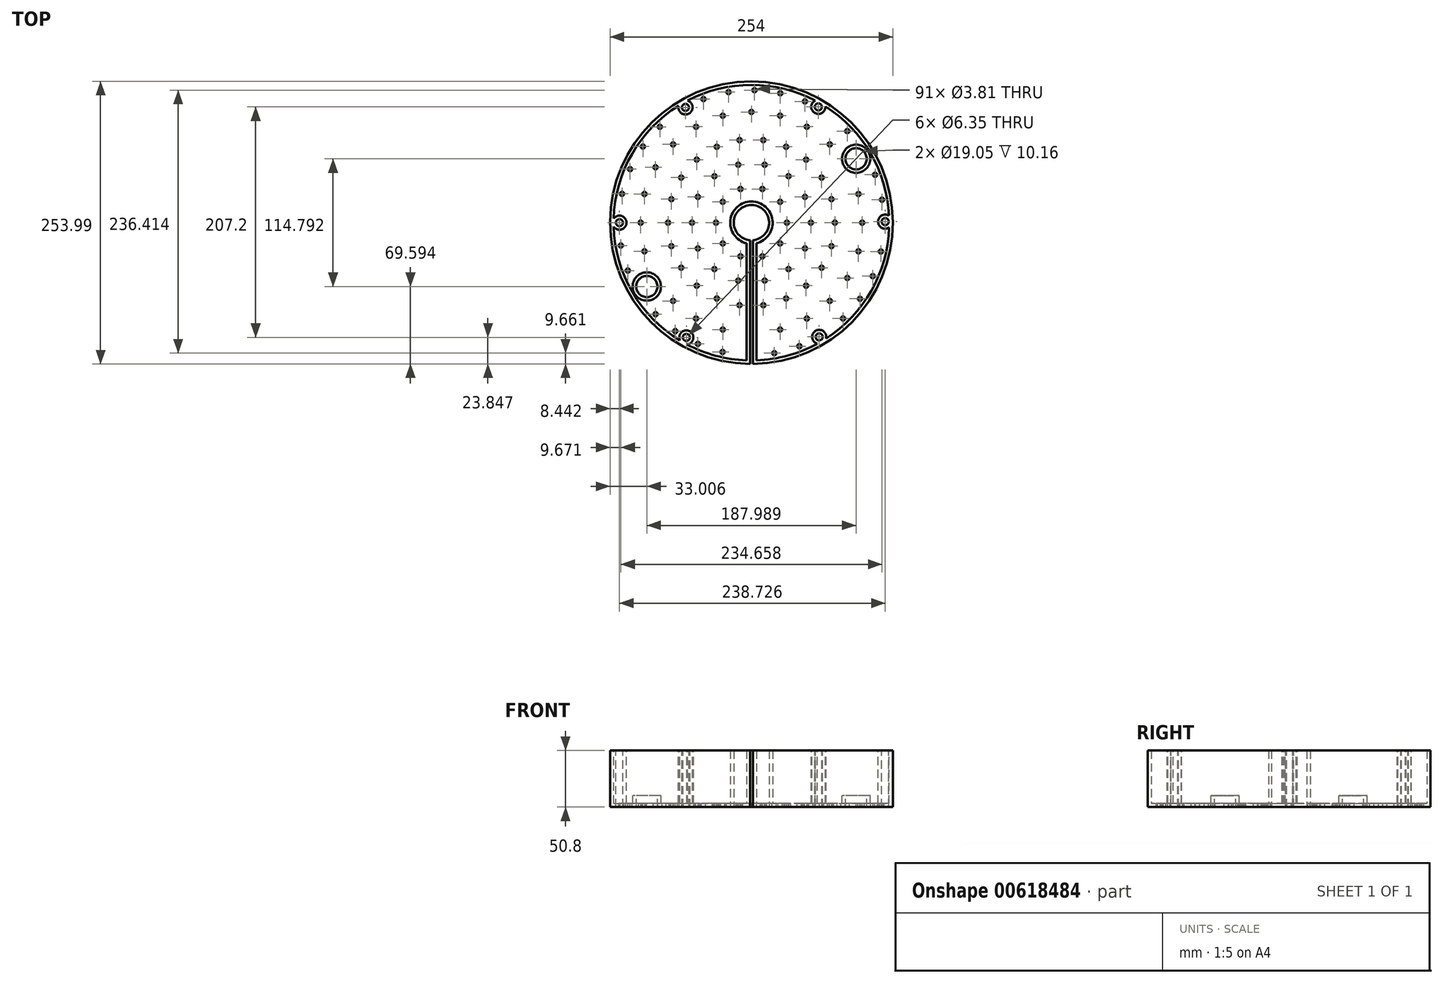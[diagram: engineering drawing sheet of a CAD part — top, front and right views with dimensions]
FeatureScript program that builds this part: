
annotation { "Feature Type Name" : "Feature", "Feature Type Description" : "" }
export const myFeature = defineFeature(function(context is Context, id is Id, definition is map)
    precondition{}
    {
        {
            var Q0;
            Q0=qCreatedBy(makeId("Top.planeOp"),FACE);
            var sketch = newSketch(context, id + "F0", { "sketchPlane" : qUnion([Q0])});
            skLineSegment(sketch, "E0.left", {"start": v(0, 0) * mm, "end": v(0, 0) * mm});
            skArc(sketch, "E1", {"start": v(1.27, -127) * mm, "mid": v(0, 127) * mm, "end": v(-1.27, -127) * mm});
            skArc(sketch, "E2", {"start": v(1.27, -15.82) * mm, "mid": v(0, 15.87) * mm, "end": v(-1.27, -15.82) * mm});
            skLineSegment(sketch, "E3", {"start": v(0, 0) * mm, "end": v(0, -127) * mm, "construction": true});
            skLineSegment(sketch, "E4", {"start": v(-1.27, -15.82) * mm, "end": v(-1.27, -127) * mm});
            skLineSegment(sketch, "E5", {"start": v(1.27, -15.82) * mm, "end": v(1.27, -127) * mm});
            skSolve(sketch);
        }
        {
            var Q0;
            Q0 = qSketchRegion(id + "F0", true);
            extrude(context, id + "F1", {"entities" : qUnion([Q0]), "depth" : 50.8 * mm, "offsetDistance" : 25.4 * mm});
        }
        {
            var Q0;
            Q0=makeQuery(id+"F1.opExtrude","CAP_FACE",FACE,{"disambiguationData":[OSD([sQuery(id+"F0.wireOp",EDGE,"E1"),sQuery(id+"F0.wireOp",EDGE,"E2"),sQuery(id+"F0.wireOp",EDGE,"E4"),sQuery(id+"F0.wireOp",EDGE,"E5")])],"isStart":false});
            var sketch = newSketch(context, id + "F2", { "sketchPlane" : qUnion([Q0])});
            skPoint(sketch, "E6", {"position": v(-118.56, 0) * mm});
            skPoint(sketch, "E7.1.0", {"position": v(-58.48, -103.14) * mm});
            skPoint(sketch, "E7.2.0", {"position": v(60.88, -102.69) * mm});
            skPoint(sketch, "E7.3.0", {"position": v(120.17, 0.91) * mm});
            skPoint(sketch, "E7.4.0", {"position": v(60.09, 104.06) * mm});
            skPoint(sketch, "E7.5.0", {"position": v(-59.27, 103.6) * mm});
            skPoint(sketch, "E7.center", {"position": v(0.8, 0.46) * mm});
            skPoint(sketch, "E8.center", {"position": v(0, 0) * mm});
            skSolve(sketch);
        }
        {
            var Q0;
            Q0=sQuery(id+"F2.wireOp",VERTEX,"E6");
            var Q1;
            Q1=sQuery(id+"F2.wireOp",VERTEX,"E7.5.0");
            var Q2;
            Q2=sQuery(id+"F2.wireOp",VERTEX,"E7.4.0");
            var Q3;
            Q3=sQuery(id+"F2.wireOp",VERTEX,"E7.3.0");
            var Q4;
            Q4=sQuery(id+"F2.wireOp",VERTEX,"E7.2.0");
            var Q5;
            Q5=sQuery(id+"F2.wireOp",VERTEX,"E7.1.0");
            var Q6;
            Q6=makeQuery(id+"F1.opExtrude","SWEPT_BODY",BODY,{"disambiguationData":[OSD([sQuery(id+"F0.wireOp",EDGE,"E1"),sQuery(id+"F0.wireOp",EDGE,"E2"),sQuery(id+"F0.wireOp",EDGE,"E4"),sQuery(id+"F0.wireOp",EDGE,"E5")])]});
            hole(context, id + "F3", {"style" : HoleStyle.SIMPLE, "endStyle" : HoleEndStyle.THROUGH, "holeDiameter" : 6.35 * mm, "majorDiameter" : 6.35 * mm, "isTappedThrough" : true, "tappedDepth" : 12.7 * mm, "tapClearance" : 3, "startFromSketch" : true, "locations" : qUnion([Q0, Q1, Q2, Q3, Q4, Q5]), "scope" : qUnion([Q6])});
        }
        {
            var Q0;
            Q0=makeQuery(id+"F1.opExtrude","CAP_FACE",FACE,{"disambiguationData":[OSD([sQuery(id+"F0.wireOp",EDGE,"E1"),sQuery(id+"F0.wireOp",EDGE,"E2"),sQuery(id+"F0.wireOp",EDGE,"E4"),sQuery(id+"F0.wireOp",EDGE,"E5")])],"isStart":false});
            var sketch = newSketch(context, id + "F4", { "sketchPlane" : qUnion([Q0])});
            skPoint(sketch, "E9", {"position": v(-94, -57.4) * mm});
            skPoint(sketch, "E10.1.0", {"position": v(94, 57.4) * mm});
            skPoint(sketch, "E10.center", {"position": v(0, 0) * mm});
            skSolve(sketch);
        }
        {
            var Q0;
            Q0=sQuery(id+"F4.wireOp",VERTEX,"E9");
            var Q1;
            Q1=sQuery(id+"F4.wireOp",VERTEX,"E10.1.0");
            var Q2;
            Q2=makeQuery(id+"F1.opExtrude","SWEPT_BODY",BODY,{"disambiguationData":[OSD([sQuery(id+"F0.wireOp",EDGE,"E1"),sQuery(id+"F0.wireOp",EDGE,"E2"),sQuery(id+"F0.wireOp",EDGE,"E4"),sQuery(id+"F0.wireOp",EDGE,"E5")])]});
            hole(context, id + "F5", {"style" : HoleStyle.SIMPLE, "endStyle" : HoleEndStyle.THROUGH, "holeDiameter" : 19.05 * mm, "majorDiameter" : 6.35 * mm, "isTappedThrough" : true, "tappedDepth" : 12.7 * mm, "tapClearance" : 3, "startFromSketch" : true, "locations" : qUnion([Q0, Q1]), "scope" : qUnion([Q2])});
        }
        {
            var Q0;
            Q0=makeQuery(id+"F1.opExtrude","CAP_FACE",FACE,{"disambiguationData":[OSD([sQuery(id+"F0.wireOp",EDGE,"E1"),sQuery(id+"F0.wireOp",EDGE,"E2"),sQuery(id+"F0.wireOp",EDGE,"E4"),sQuery(id+"F0.wireOp",EDGE,"E5")])],"isStart":false});
            shell(context, id + "F6", {"entities" : qUnion([Q0]), "thickness" : 3.17 * mm});
        }
        {
            var Q0;
            {var subQ0=sQuery(id+"F0.wireOp",EDGE,"E5");var subQ1=sQuery(id+"F0.wireOp",EDGE,"E4");var subQ2=sQuery(id+"F0.wireOp",EDGE,"E2");var subQ3=sQuery(id+"F0.wireOp",EDGE,"E1");Q0=makeQuery(id+"F6.opShell","OFFSET_FACE",FACE,{"disambiguationData":[OSD([subQ3,subQ2,subQ1,subQ0]),TDD([makeQuery(id+"F1.opExtrude","CAP_FACE",FACE,{"disambiguationData":[OSD([subQ3,subQ2,subQ1,subQ0])],"isStart":false})]),OD(0.0)]});}
            var Q1;
            {var subQ0=sQuery(id+"F0.wireOp",EDGE,"E5");var subQ1=sQuery(id+"F0.wireOp",EDGE,"E4");var subQ2=sQuery(id+"F0.wireOp",EDGE,"E2");var subQ3=sQuery(id+"F0.wireOp",EDGE,"E1");Q1=makeQuery(id+"F6.opShell","OFFSET_FACE",FACE,{"disambiguationData":[OSD([subQ3,subQ2,subQ1,subQ0]),TDD([makeQuery(id+"F1.opExtrude","CAP_FACE",FACE,{"disambiguationData":[OSD([subQ3,subQ2,subQ1,subQ0])],"isStart":false})]),OD(1.0)]});}
            extrude(context, id + "F7", {"entities" : qUnion([Q0, Q1]), "operationType" : NewBodyOperationType.REMOVE, "oppositeDirection" : true, "depth" : 25.4 * mm, "offsetDistance" : 25.4 * mm});
        }
        {
            var Q0;
            {var subQ0=sQuery(id+"F0.wireOp",EDGE,"E5");var subQ1=sQuery(id+"F0.wireOp",EDGE,"E4");var subQ2=sQuery(id+"F0.wireOp",EDGE,"E2");var subQ3=sQuery(id+"F0.wireOp",EDGE,"E1");Q0=makeQuery(id+"F7.boolean.opBoolean","COPY",FACE,{"derivedFrom":makeQuery(id+"F7.opExtrude","CAP_FACE",FACE,{"disambiguationData":[OSD([subQ3,subQ2,subQ1,subQ0]),TDD([makeQuery(id+"F6.opShell","OFFSET_FACE",FACE,{"disambiguationData":[OSD([subQ3,subQ2,subQ1,subQ0]),TDD([makeQuery(id+"F1.opExtrude","CAP_FACE",FACE,{"disambiguationData":[OSD([subQ3,subQ2,subQ1,subQ0])],"isStart":false})]),OD(0.0)]})])],"isStart":false})});}
            var Q1;
            {var subQ0=sQuery(id+"F0.wireOp",EDGE,"E5");var subQ1=sQuery(id+"F0.wireOp",EDGE,"E4");var subQ2=sQuery(id+"F0.wireOp",EDGE,"E2");var subQ3=sQuery(id+"F0.wireOp",EDGE,"E1");Q1=makeQuery(id+"F7.boolean.opBoolean","COPY",FACE,{"derivedFrom":makeQuery(id+"F7.opExtrude","CAP_FACE",FACE,{"disambiguationData":[OSD([subQ3,subQ2,subQ1,subQ0]),TDD([makeQuery(id+"F6.opShell","OFFSET_FACE",FACE,{"disambiguationData":[OSD([subQ3,subQ2,subQ1,subQ0]),TDD([makeQuery(id+"F1.opExtrude","CAP_FACE",FACE,{"disambiguationData":[OSD([subQ3,subQ2,subQ1,subQ0])],"isStart":false})]),OD(1.0)]})])],"isStart":false})});}
            extrude(context, id + "F8", {"entities" : qUnion([Q0, Q1]), "operationType" : NewBodyOperationType.REMOVE, "oppositeDirection" : true, "depth" : 15.24 * mm, "offsetDistance" : 25.4 * mm});
        }
        {
            var Q0;
            {var subQ0=sQuery(id+"F0.wireOp",EDGE,"E5");var subQ1=sQuery(id+"F0.wireOp",EDGE,"E4");var subQ2=sQuery(id+"F0.wireOp",EDGE,"E2");var subQ3=sQuery(id+"F0.wireOp",EDGE,"E1");Q0=makeQuery(id+"F6.opShell","OFFSET_FACE",FACE,{"disambiguationData":[OSD([subQ3,subQ2,subQ1,subQ0]),TDD([makeQuery(id+"F1.opExtrude","CAP_FACE",FACE,{"disambiguationData":[OSD([subQ3,subQ2,subQ1,subQ0])],"isStart":true})])]});}
            var sketch = newSketch(context, id + "F9", { "sketchPlane" : qUnion([Q0])});
            skPoint(sketch, "E11", {"position": v(-31.83, 0) * mm});
            skPoint(sketch, "E12.1.0", {"position": v(-25.75, -18.71) * mm});
            skPoint(sketch, "E12.2.0", {"position": v(-9.84, -30.27) * mm});
            skPoint(sketch, "E12.3.0", {"position": v(9.84, -30.27) * mm});
            skPoint(sketch, "E12.4.0", {"position": v(25.75, -18.71) * mm});
            skPoint(sketch, "E12.5.0", {"position": v(31.83, 0) * mm});
            skPoint(sketch, "E12.6.0", {"position": v(25.75, 18.71) * mm});
            skPoint(sketch, "E12.7.0", {"position": v(9.84, 30.27) * mm});
            skPoint(sketch, "E12.8.0", {"position": v(-9.84, 30.27) * mm});
            skPoint(sketch, "E12.center", {"position": v(0, 0) * mm});
            skPoint(sketch, "E13.0.9.0", {"position": v(-25.75, 18.71) * mm});
            skPoint(sketch, "E14", {"position": v(-53.39, 0) * mm});
            skPoint(sketch, "E15.1.0", {"position": v(-48.1, -23.16) * mm});
            skPoint(sketch, "E15.2.0", {"position": v(-33.29, -41.74) * mm});
            skPoint(sketch, "E15.3.0", {"position": v(-11.88, -52.05) * mm});
            skPoint(sketch, "E15.4.0", {"position": v(11.88, -52.05) * mm});
            skPoint(sketch, "E15.5.0", {"position": v(33.29, -41.74) * mm});
            skPoint(sketch, "E15.6.0", {"position": v(48.1, -23.16) * mm});
            skPoint(sketch, "E15.7.0", {"position": v(53.39, 0) * mm});
            skPoint(sketch, "E15.8.0", {"position": v(48.1, 23.16) * mm});
            skPoint(sketch, "E15.9.0", {"position": v(33.29, 41.74) * mm});
            skPoint(sketch, "E15.10.0", {"position": v(11.88, 52.05) * mm});
            skPoint(sketch, "E15.11.0", {"position": v(-11.88, 52.05) * mm});
            skPoint(sketch, "E15.12.0", {"position": v(-33.29, 41.74) * mm});
            skPoint(sketch, "E15.13.0", {"position": v(-48.1, 23.16) * mm});
            skPoint(sketch, "E16", {"position": v(-74.94, 0) * mm});
            skPoint(sketch, "E17.1.0", {"position": v(-71.9, -21.11) * mm});
            skPoint(sketch, "E17.2.0", {"position": v(-63.05, -40.52) * mm});
            skPoint(sketch, "E17.3.0", {"position": v(-49.08, -56.64) * mm});
            skPoint(sketch, "E17.4.0", {"position": v(-31.13, -68.17) * mm});
            skPoint(sketch, "E17.5.0", {"position": v(-10.67, -74.18) * mm});
            skPoint(sketch, "E17.6.0", {"position": v(10.67, -74.18) * mm});
            skPoint(sketch, "E17.7.0", {"position": v(31.13, -68.17) * mm});
            skPoint(sketch, "E17.8.0", {"position": v(49.08, -56.64) * mm});
            skPoint(sketch, "E17.9.0", {"position": v(63.05, -40.52) * mm});
            skPoint(sketch, "E17.10.0", {"position": v(71.9, -21.11) * mm});
            skPoint(sketch, "E17.11.0", {"position": v(74.94, 0) * mm});
            skPoint(sketch, "E17.12.0", {"position": v(71.9, 21.11) * mm});
            skPoint(sketch, "E17.13.0", {"position": v(63.05, 40.52) * mm});
            skPoint(sketch, "E17.14.0", {"position": v(49.08, 56.64) * mm});
            skPoint(sketch, "E17.15.0", {"position": v(31.13, 68.17) * mm});
            skPoint(sketch, "E17.16.0", {"position": v(10.67, 74.18) * mm});
            skPoint(sketch, "E17.17.0", {"position": v(-10.67, 74.18) * mm});
            skPoint(sketch, "E17.18.0", {"position": v(-31.13, 68.17) * mm});
            skPoint(sketch, "E17.19.0", {"position": v(-49.08, 56.64) * mm});
            skPoint(sketch, "E18.0.20.0", {"position": v(-63.05, 40.52) * mm});
            skPoint(sketch, "E18.0.21.0", {"position": v(-71.9, 21.11) * mm});
            skPoint(sketch, "E19", {"position": v(-99.5, 0) * mm});
            skPoint(sketch, "E20.1.0", {"position": v(-96.12, -25.75) * mm});
            skPoint(sketch, "E20.3.0", {"position": v(-70.36, -70.36) * mm});
            skPoint(sketch, "E20.4.0", {"position": v(-49.75, -86.18) * mm});
            skPoint(sketch, "E20.5.0", {"position": v(-25.75, -96.12) * mm});
            skPoint(sketch, "E20.7.0", {"position": v(25.75, -96.12) * mm});
            skPoint(sketch, "E20.8.0", {"position": v(49.75, -86.18) * mm});
            skPoint(sketch, "E20.9.0", {"position": v(70.36, -70.36) * mm});
            skPoint(sketch, "E20.10.0", {"position": v(86.18, -49.75) * mm});
            skPoint(sketch, "E20.11.0", {"position": v(96.12, -25.75) * mm});
            skPoint(sketch, "E20.12.0", {"position": v(99.5, 0) * mm});
            skPoint(sketch, "E20.13.0", {"position": v(96.12, 25.75) * mm});
            skPoint(sketch, "E20.15.0", {"position": v(70.36, 70.36) * mm});
            skPoint(sketch, "E20.16.0", {"position": v(49.75, 86.18) * mm});
            skPoint(sketch, "E20.17.0", {"position": v(25.75, 96.12) * mm});
            skPoint(sketch, "E20.18.0", {"position": v(0, 99.5) * mm});
            skPoint(sketch, "E20.19.0", {"position": v(-25.75, 96.12) * mm});
            skPoint(sketch, "E20.20.0", {"position": v(-49.75, 86.18) * mm});
            skPoint(sketch, "E20.21.0", {"position": v(-70.36, 70.36) * mm});
            skPoint(sketch, "E20.22.0", {"position": v(-86.18, 49.75) * mm});
            skPoint(sketch, "E20.23.0", {"position": v(-96.12, 25.75) * mm});
            skPoint(sketch, "E21.1.0", {"position": v(-117.33, -20.56) * mm});
            skPoint(sketch, "E21.2.0", {"position": v(-111.06, -43.05) * mm});
            skPoint(sketch, "E21.4.0", {"position": v(-86.13, -82.28) * mm});
            skPoint(sketch, "E21.5.0", {"position": v(-68.43, -97.5) * mm});
            skPoint(sketch, "E21.6.0", {"position": v(-48.1, -108.98) * mm});
            skPoint(sketch, "E21.7.0", {"position": v(-25.9, -116.26) * mm});
            skPoint(sketch, "E21.9.0", {"position": v(20.56, -117.33) * mm});
            skPoint(sketch, "E21.10.0", {"position": v(43.05, -111.06) * mm});
            skPoint(sketch, "E21.12.0", {"position": v(82.28, -86.13) * mm});
            skPoint(sketch, "E21.13.0", {"position": v(97.5, -68.43) * mm});
            skPoint(sketch, "E21.14.0", {"position": v(108.98, -48.1) * mm});
            skPoint(sketch, "E21.15.0", {"position": v(116.26, -25.9) * mm});
            skPoint(sketch, "E21.17.0", {"position": v(117.33, 20.56) * mm});
            skPoint(sketch, "E21.18.0", {"position": v(111.06, 43.05) * mm});
            skPoint(sketch, "E21.20.0", {"position": v(86.13, 82.28) * mm});
            skPoint(sketch, "E21.22.0", {"position": v(48.1, 108.98) * mm});
            skPoint(sketch, "E21.23.0", {"position": v(25.9, 116.26) * mm});
            skPoint(sketch, "E21.24.0", {"position": v(2.73, 119.09) * mm});
            skPoint(sketch, "E21.25.0", {"position": v(-20.56, 117.33) * mm});
            skPoint(sketch, "E21.26.0", {"position": v(-43.05, 111.06) * mm});
            skPoint(sketch, "E21.28.0", {"position": v(-82.28, 86.13) * mm});
            skPoint(sketch, "E21.29.0", {"position": v(-97.5, 68.43) * mm});
            skPoint(sketch, "E21.30.0", {"position": v(-108.98, 48.1) * mm});
            skPoint(sketch, "E21.31.0", {"position": v(-116.26, 25.9) * mm});
            skSolve(sketch);
        }
        {
            var Q0;
            Q0=sQuery(id+"F9.wireOp",VERTEX,"E19");
            var Q1;
            Q1=sQuery(id+"F9.wireOp",VERTEX,"E21.31.0");
            var Q2;
            Q2=sQuery(id+"F9.wireOp",VERTEX,"E20.23.0");
            var Q3;
            Q3=sQuery(id+"F9.wireOp",VERTEX,"E20.22.0");
            var Q4;
            Q4=sQuery(id+"F9.wireOp",VERTEX,"E21.30.0");
            var Q5;
            Q5=sQuery(id+"F9.wireOp",VERTEX,"E21.29.0");
            var Q6;
            Q6=sQuery(id+"F9.wireOp",VERTEX,"E20.21.0");
            var Q7;
            Q7=sQuery(id+"F9.wireOp",VERTEX,"E21.28.0");
            var Q8;
            Q8=sQuery(id+"F9.wireOp",VERTEX,"E20.20.0");
            var Q9;
            Q9=sQuery(id+"F9.wireOp",VERTEX,"E21.26.0");
            var Q10;
            Q10=sQuery(id+"F9.wireOp",VERTEX,"E21.25.0");
            var Q11;
            Q11=sQuery(id+"F9.wireOp",VERTEX,"E21.24.0");
            var Q12;
            Q12=sQuery(id+"F9.wireOp",VERTEX,"E21.23.0");
            var Q13;
            Q13=sQuery(id+"F9.wireOp",VERTEX,"E21.22.0");
            var Q14;
            Q14=sQuery(id+"F9.wireOp",VERTEX,"E21.20.0");
            var Q15;
            Q15=sQuery(id+"F9.wireOp",VERTEX,"E20.15.0");
            var Q16;
            Q16=sQuery(id+"F9.wireOp",VERTEX,"E20.16.0");
            var Q17;
            Q17=sQuery(id+"F9.wireOp",VERTEX,"E20.17.0");
            var Q18;
            Q18=sQuery(id+"F9.wireOp",VERTEX,"E20.18.0");
            var Q19;
            Q19=sQuery(id+"F9.wireOp",VERTEX,"E20.19.0");
            var Q20;
            Q20=sQuery(id+"F9.wireOp",VERTEX,"E16");
            var Q21;
            Q21=sQuery(id+"F9.wireOp",VERTEX,"E14");
            var Q22;
            Q22=sQuery(id+"F9.wireOp",VERTEX,"E11");
            var Q23;
            Q23=sQuery(id+"F9.wireOp",VERTEX,"E12.5.0");
            var Q24;
            Q24=sQuery(id+"F9.wireOp",VERTEX,"E15.7.0");
            var Q25;
            Q25=sQuery(id+"F9.wireOp",VERTEX,"E17.11.0");
            var Q26;
            Q26=sQuery(id+"F9.wireOp",VERTEX,"E20.12.0");
            var Q27;
            Q27=sQuery(id+"F9.wireOp",VERTEX,"E21.17.0");
            var Q28;
            Q28=sQuery(id+"F9.wireOp",VERTEX,"E20.13.0");
            var Q29;
            Q29=sQuery(id+"F9.wireOp",VERTEX,"E21.18.0");
            var Q30;
            Q30=sQuery(id+"F9.wireOp",VERTEX,"E17.12.0");
            var Q31;
            Q31=sQuery(id+"F9.wireOp",VERTEX,"E17.13.0");
            var Q32;
            Q32=sQuery(id+"F9.wireOp",VERTEX,"E15.8.0");
            var Q33;
            Q33=sQuery(id+"F9.wireOp",VERTEX,"E12.6.0");
            var Q34;
            Q34=sQuery(id+"F9.wireOp",VERTEX,"E12.7.0");
            var Q35;
            Q35=sQuery(id+"F9.wireOp",VERTEX,"E15.9.0");
            var Q36;
            Q36=sQuery(id+"F9.wireOp",VERTEX,"E17.14.0");
            var Q37;
            Q37=sQuery(id+"F9.wireOp",VERTEX,"E17.15.0");
            var Q38;
            Q38=sQuery(id+"F9.wireOp",VERTEX,"E17.16.0");
            var Q39;
            Q39=sQuery(id+"F9.wireOp",VERTEX,"E15.10.0");
            var Q40;
            Q40=sQuery(id+"F9.wireOp",VERTEX,"E17.17.0");
            var Q41;
            Q41=sQuery(id+"F9.wireOp",VERTEX,"E15.11.0");
            var Q42;
            Q42=sQuery(id+"F9.wireOp",VERTEX,"E12.8.0");
            var Q43;
            Q43=sQuery(id+"F9.wireOp",VERTEX,"E13.0.9.0");
            var Q44;
            Q44=sQuery(id+"F9.wireOp",VERTEX,"E15.13.0");
            var Q45;
            Q45=sQuery(id+"F9.wireOp",VERTEX,"E15.12.0");
            var Q46;
            Q46=sQuery(id+"F9.wireOp",VERTEX,"E17.18.0");
            var Q47;
            Q47=sQuery(id+"F9.wireOp",VERTEX,"E17.19.0");
            var Q48;
            Q48=sQuery(id+"F9.wireOp",VERTEX,"E18.0.20.0");
            var Q49;
            Q49=sQuery(id+"F9.wireOp",VERTEX,"E18.0.21.0");
            var Q50;
            Q50=sQuery(id+"F9.wireOp",VERTEX,"E21.1.0");
            var Q51;
            Q51=sQuery(id+"F9.wireOp",VERTEX,"E21.2.0");
            var Q52;
            Q52=sQuery(id+"F9.wireOp",VERTEX,"E20.1.0");
            var Q53;
            Q53=sQuery(id+"F9.wireOp",VERTEX,"E21.4.0");
            var Q54;
            Q54=sQuery(id+"F9.wireOp",VERTEX,"E21.5.0");
            var Q55;
            Q55=sQuery(id+"F9.wireOp",VERTEX,"E21.6.0");
            var Q56;
            Q56=sQuery(id+"F9.wireOp",VERTEX,"E21.7.0");
            var Q57;
            Q57=sQuery(id+"F9.wireOp",VERTEX,"E20.5.0");
            var Q58;
            Q58=sQuery(id+"F9.wireOp",VERTEX,"E17.5.0");
            var Q59;
            Q59=sQuery(id+"F9.wireOp",VERTEX,"E15.3.0");
            var Q60;
            Q60=sQuery(id+"F9.wireOp",VERTEX,"E12.2.0");
            var Q61;
            Q61=sQuery(id+"F9.wireOp",VERTEX,"E12.1.0");
            var Q62;
            Q62=sQuery(id+"F9.wireOp",VERTEX,"E15.2.0");
            var Q63;
            Q63=sQuery(id+"F9.wireOp",VERTEX,"E17.4.0");
            var Q64;
            Q64=sQuery(id+"F9.wireOp",VERTEX,"E20.4.0");
            var Q65;
            Q65=sQuery(id+"F9.wireOp",VERTEX,"E20.3.0");
            var Q66;
            Q66=sQuery(id+"F9.wireOp",VERTEX,"E17.3.0");
            var Q67;
            Q67=sQuery(id+"F9.wireOp",VERTEX,"E17.2.0");
            var Q68;
            Q68=sQuery(id+"F9.wireOp",VERTEX,"E17.1.0");
            var Q69;
            Q69=sQuery(id+"F9.wireOp",VERTEX,"E15.1.0");
            var Q70;
            Q70=sQuery(id+"F9.wireOp",VERTEX,"E12.3.0");
            var Q71;
            Q71=sQuery(id+"F9.wireOp",VERTEX,"E15.4.0");
            var Q72;
            Q72=sQuery(id+"F9.wireOp",VERTEX,"E17.6.0");
            var Q73;
            Q73=sQuery(id+"F9.wireOp",VERTEX,"E21.9.0");
            var Q74;
            Q74=sQuery(id+"F9.wireOp",VERTEX,"E20.7.0");
            var Q75;
            Q75=sQuery(id+"F9.wireOp",VERTEX,"E21.10.0");
            var Q76;
            Q76=sQuery(id+"F9.wireOp",VERTEX,"E20.8.0");
            var Q77;
            Q77=sQuery(id+"F9.wireOp",VERTEX,"E21.12.0");
            var Q78;
            Q78=sQuery(id+"F9.wireOp",VERTEX,"E20.9.0");
            var Q79;
            Q79=sQuery(id+"F9.wireOp",VERTEX,"E21.13.0");
            var Q80;
            Q80=sQuery(id+"F9.wireOp",VERTEX,"E20.10.0");
            var Q81;
            Q81=sQuery(id+"F9.wireOp",VERTEX,"E21.14.0");
            var Q82;
            Q82=sQuery(id+"F9.wireOp",VERTEX,"E20.11.0");
            var Q83;
            Q83=sQuery(id+"F9.wireOp",VERTEX,"E17.10.0");
            var Q84;
            Q84=sQuery(id+"F9.wireOp",VERTEX,"E17.9.0");
            var Q85;
            Q85=sQuery(id+"F9.wireOp",VERTEX,"E17.8.0");
            var Q86;
            Q86=sQuery(id+"F9.wireOp",VERTEX,"E17.7.0");
            var Q87;
            Q87=sQuery(id+"F9.wireOp",VERTEX,"E15.5.0");
            var Q88;
            Q88=sQuery(id+"F9.wireOp",VERTEX,"E15.6.0");
            var Q89;
            Q89=sQuery(id+"F9.wireOp",VERTEX,"E12.4.0");
            var Q90;
            Q90=sQuery(id+"F9.wireOp",VERTEX,"E17.8.0");
            var Q91;
            Q91=sQuery(id+"F9.wireOp",VERTEX,"E17.7.0");
            var Q92;
            Q92=sQuery(id+"F9.wireOp",VERTEX,"E17.9.0");
            var Q93;
            Q93=sQuery(id+"F9.wireOp",VERTEX,"E17.10.0");
            var Q94;
            Q94=sQuery(id+"F9.wireOp",VERTEX,"E20.11.0");
            var Q95;
            Q95=sQuery(id+"F9.wireOp",VERTEX,"E15.6.0");
            var Q96;
            Q96=sQuery(id+"F9.wireOp",VERTEX,"E21.15.0");
            var Q97;
            Q97=sQuery(id+"F9.wireOp",VERTEX,"E15.5.0");
            var Q98;
            Q98=sQuery(id+"F9.wireOp",VERTEX,"E12.4.0");
            var Q99;
            Q99=makeQuery(id+"F1.opExtrude","SWEPT_BODY",BODY,{"disambiguationData":[OSD([sQuery(id+"F0.wireOp",EDGE,"E1"),sQuery(id+"F0.wireOp",EDGE,"E2"),sQuery(id+"F0.wireOp",EDGE,"E4"),sQuery(id+"F0.wireOp",EDGE,"E5")])]});
            hole(context, id + "F10", {"style" : HoleStyle.SIMPLE, "endStyle" : HoleEndStyle.THROUGH, "holeDiameter" : 3.8 * mm, "majorDiameter" : 6.35 * mm, "isTappedThrough" : true, "tappedDepth" : 12.7 * mm, "tapClearance" : 3, "startFromSketch" : true, "locations" : qUnion([Q0, Q1, Q2, Q3, Q4, Q5, Q6, Q7, Q8, Q9, Q10, Q11, Q12, Q13, Q14, Q15, Q16, Q17, Q18, Q19, Q20, Q21, Q22, Q23, Q24, Q25, Q26, Q27, Q28, Q29, Q30, Q31, Q32, Q33, Q34, Q35, Q36, Q37, Q38, Q39, Q40, Q41, Q42, Q43, Q44, Q45, Q46, Q47, Q48, Q49, Q50, Q51, Q52, Q53, Q54, Q55, Q56, Q57, Q58, Q59, Q60, Q61, Q62, Q63, Q64, Q65, Q66, Q67, Q68, Q69, Q70, Q71, Q72, Q73, Q74, Q75, Q76, Q77, Q78, Q79, Q80, Q81, Q82, Q83, Q84, Q85, Q86, Q87, Q88, Q89, Q90, Q91, Q92, Q93, Q94, Q95, Q96, Q97, Q98]), "scope" : qUnion([Q99])});
        }
        {
            var Q0;
            Q0=makeQuery(id+"F1.opExtrude","CAP_FACE",FACE,{"disambiguationData":[OSD([sQuery(id+"F0.wireOp",EDGE,"E1"),sQuery(id+"F0.wireOp",EDGE,"E2"),sQuery(id+"F0.wireOp",EDGE,"E4"),sQuery(id+"F0.wireOp",EDGE,"E5")])],"isStart":false});
            var sketch = newSketch(context, id + "F11", { "sketchPlane" : qUnion([Q0])});
            skCircle(sketch, "E22", {"center": v(1.27, 0) * mm, "radius": 133.35 * mm});
            skSolve(sketch);
        }
        {
            var Q0;
            Q0=makeQuery(id+"F11.imprint","IMPRINT",FACE,{"disambiguationData":[TD([[makeQuery(id+"F11.imprint","IMPRINT",EDGE,{"derivedFrom":sQuery(id+"F11.wireOp",EDGE,"E22")}),1.0]])]});
            var Q1;
            Q1=sQuery(id+"F11.wireOp",EDGE,"E22");
            extrude(context, id + "F12", {"entities" : qUnion([Q0]), "surfaceEntities" : qUnion([Q1]), "depth" : 6.35 * mm, "offsetDistance" : 25.4 * mm});
        }
        {
            var Q0;
            Q0=makeQuery(id+"F12.opExtrude","SWEPT_BODY",BODY,{"disambiguationData":[OSD([sQuery(id+"F0.wireOp",EDGE,"E1"),sQuery(id+"F0.wireOp",EDGE,"E2"),sQuery(id+"F0.wireOp",EDGE,"E4"),sQuery(id+"F0.wireOp",EDGE,"E5"),sQuery(id+"F11.wireOp",EDGE,"E22")])]});
            deleteBodies(context, id + "F13", {"entities" : qUnion([Q0])});
        }
    });
